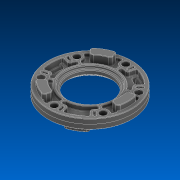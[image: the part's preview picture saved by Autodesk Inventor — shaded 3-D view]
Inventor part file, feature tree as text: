
AUTODESK INVENTOR PART (.ipt)
format: ipt  version: 2022.2 (Build 262287000, 287)  size: 1,735,680 bytes
history: native  units: in
note: dims shown in document units (in); Inventor stores cm internally (conversion verified against a paired STEP export)
features: fillet x1
ambient origin geometry x8: Origin, YZ Plane, XZ Plane, XY Plane, X Axis, Y Axis, Z Axis, Center Point
bodies: Solid1 (feature_tree)
feature tree (1):
  fillet  "Fillet10"  [1 undecoded]
note: 1 required parameter value undecoded (feature->parameter linkage not recoverable at this tier; creation-order binding heuristic only, values carry confidence <= 0.55)
